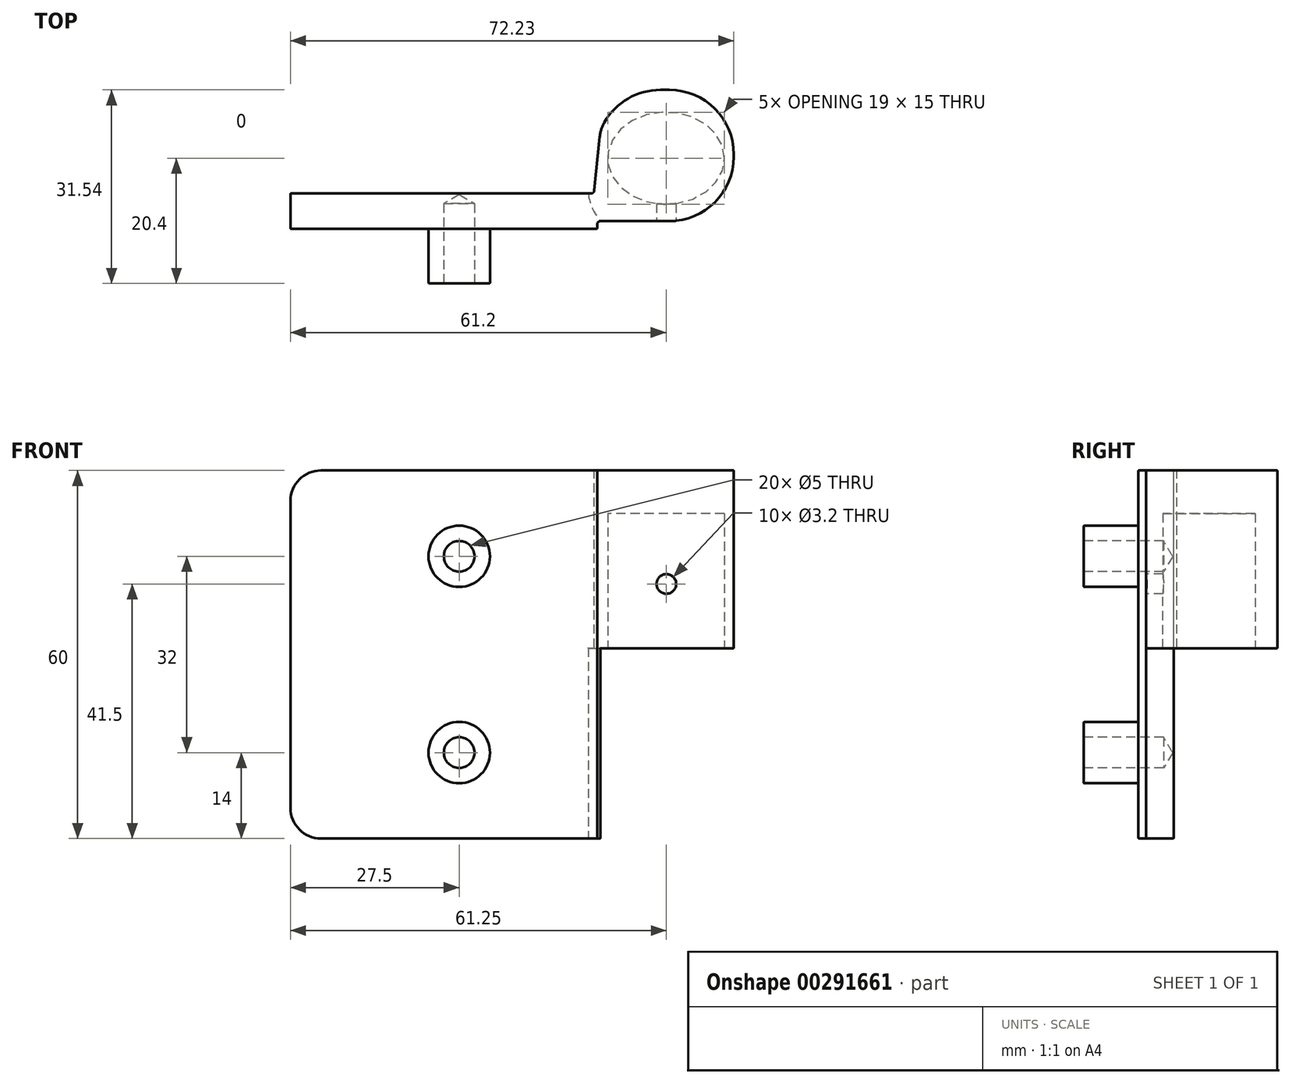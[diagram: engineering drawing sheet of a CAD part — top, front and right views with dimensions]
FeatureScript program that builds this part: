
annotation { "Feature Type Name" : "Feature", "Feature Type Description" : "" }
export const myFeature = defineFeature(function(context is Context, id is Id, definition is map)
    precondition{}
    {
        {
            var Q0;
            Q0=qCreatedBy(makeId("Front.planeOp"),FACE);
            var sketch = newSketch(context, id + "F0", { "sketchPlane" : qUnion([Q0])});
            skLineSegment(sketch, "E0", {"start": v(0, 0) * mm, "end": v(-48.5, 0) * mm});
            skLineSegment(sketch, "E1", {"start": v(-48.5, 0) * mm, "end": v(-48.5, -5.75) * mm});
            skLineSegment(sketch, "E2", {"start": v(-48.5, -5.75) * mm, "end": v(1.5, -5.75) * mm});
            skLineSegment(sketch, "E3", {"start": v(1.5, -5.75) * mm, "end": v(1.5, -5) * mm});
            skLineSegment(sketch, "E4", {"start": v(2, -4.5) * mm, "end": v(3.23, -4.5) * mm});
            skLineSegment(sketch, "E5", {"start": v(3.23, -4.5) * mm, "end": v(13.23, -4.5) * mm});
            skLineSegment(sketch, "E6", {"start": v(23.73, 6) * mm, "end": v(23.73, 6.4) * mm});
            skLineSegment(sketch, "E7", {"start": v(13.23, 16.9) * mm, "end": v(11.78, 16.9) * mm});
            skLineSegment(sketch, "E8", {"start": v(0.5, 0) * mm, "end": v(0, 0) * mm});
            skArc(sketch, "E9.filletArc", {"start": v(13.23, -4.5) * mm, "mid": v(20.66, -1.43) * mm, "end": v(23.73, 6) * mm});
            skArc(sketch, "E10.filletArc", {"start": v(23.73, 6.4) * mm, "mid": v(20.66, 13.82) * mm, "end": v(13.23, 16.9) * mm});
            skArc(sketch, "E11.filletArc", {"start": v(11.78, 16.9) * mm, "mid": v(6.5, 15.47) * mm, "end": v(2.65, 11.6) * mm});
            skArc(sketch, "E12.filletArc", {"start": v(0.5, 0) * mm, "mid": v(0.85, 0.15) * mm, "end": v(1, 0.5) * mm});
            skPoint(sketch, "E13.visualSharp", {"position": v(1.5, -4.5) * mm});
            skArc(sketch, "E13.filletArc", {"start": v(2, -4.5) * mm, "mid": v(1.65, -4.66) * mm, "end": v(1.5, -5) * mm});
            skLineSegment(sketch, "E14", {"start": v(1, 0.5) * mm, "end": v(1.9, 9.23) * mm});
            skPoint(sketch, "E15.visualSharp", {"position": v(2, 10.22) * mm});
            skArc(sketch, "E15.filletArc", {"start": v(2.65, 11.6) * mm, "mid": v(2.15, 10.45) * mm, "end": v(1.9, 9.23) * mm});
            skSolve(sketch);
        }
        {
            var Q0;
            Q0=makeQuery(id+"F0.imprint","IMPRINT",FACE,{"disambiguationData":[TD([[makeQuery(id+"F0.imprint","IMPRINT",EDGE,{"derivedFrom":sQuery(id+"F0.wireOp",EDGE,"E0")}),1.0]])]});
            extrude(context, id + "F1", {"entities" : qUnion([Q0]), "depth" : 60 * mm});
        }
        {
            var Q0;
            Q0=makeQuery(id+"F1.opExtrude","CAP_EDGE",EDGE,{"disambiguationData":[OSD([sQuery(id+"F0.wireOp",EDGE,"E1")])],"isStart":false});
            var Q1;
            Q1=makeQuery(id+"F1.opExtrude","CAP_EDGE",EDGE,{"disambiguationData":[OSD([sQuery(id+"F0.wireOp",EDGE,"E1")])],"isStart":true});
            fillet(context, id + "F2", {"entities" : qUnion([Q0, Q1]), "radius" : 5 * mm, "tangentPropagation" : true, "allowEdgeOverflow" : false});
        }
        {
            var Q0;
            Q0=makeQuery(id+"F1.opExtrude","SWEPT_FACE",FACE,{"disambiguationData":[OSD([sQuery(id+"F0.wireOp",EDGE,"E4"),sQuery(id+"F0.wireOp",EDGE,"E5")])]});
            var sketch = newSketch(context, id + "F3", { "sketchPlane" : qUnion([Q0])});
            skLineSegment(sketch, "E16.bottom", {"start": v(2, 60) * mm, "end": v(31.94, 60) * mm});
            skLineSegment(sketch, "E16.top", {"start": v(2, 29) * mm, "end": v(31.94, 29) * mm});
            skLineSegment(sketch, "E16.left", {"start": v(2, 60) * mm, "end": v(2, 29) * mm});
            skLineSegment(sketch, "E16.right", {"start": v(31.94, 60) * mm, "end": v(31.94, 29) * mm});
            skSolve(sketch);
        }
        {
            var Q0;
            Q0=qSketchRegion(id+"F3",true);
            extrude(context, id + "F4", {"entities" : qUnion([Q0]), "operationType" : NewBodyOperationType.REMOVE, "endBound" : BoundingType.THROUGH_ALL, "oppositeDirection" : true, "depth" : 25 * mm});
        }
        {
            var Q0;
            Q0=makeQuery(id+"F1.opExtrude","CAP_FACE",FACE,{"disambiguationData":[OSD([sQuery(id+"F0.wireOp",EDGE,"E0"),sQuery(id+"F0.wireOp",EDGE,"E1"),sQuery(id+"F0.wireOp",EDGE,"E2"),sQuery(id+"F0.wireOp",EDGE,"E3"),sQuery(id+"F0.wireOp",EDGE,"E4"),sQuery(id+"F0.wireOp",EDGE,"E5"),sQuery(id+"F0.wireOp",EDGE,"E6"),sQuery(id+"F0.wireOp",EDGE,"E7"),sQuery(id+"F0.wireOp",EDGE,"GG9Xp7Lx-0V8L-KjhP-dehT-RjXL1Wiv3JEy"),sQuery(id+"F0.wireOp",EDGE,"E8"),sQuery(id+"F0.wireOp",EDGE,"E9.filletArc"),sQuery(id+"F0.wireOp",EDGE,"E10.filletArc"),sQuery(id+"F0.wireOp",EDGE,"E11.filletArc"),sQuery(id+"F0.wireOp",EDGE,"E12.filletArc"),sQuery(id+"F0.wireOp",EDGE,"E13.filletArc")])],"isStart":false});
            var sketch = newSketch(context, id + "F5", { "sketchPlane" : qUnion([Q0])});
            skArc(sketch, "E17", {"start": v(0, 0) * mm, "mid": v(0.68, -2.4) * mm, "end": v(2, -4.5) * mm});
            skLineSegment(sketch, "E18", {"start": v(2, -4.5) * mm, "end": v(4.6, -0.03) * mm});
            skLineSegment(sketch, "E19", {"start": v(4.6, -0.03) * mm, "end": v(2.71, 13.2) * mm});
            skLineSegment(sketch, "E20", {"start": v(2.71, 13.2) * mm, "end": v(-1.4, 7.63) * mm});
            skLineSegment(sketch, "E21", {"start": v(0, 0) * mm, "end": v(-1.4, 7.63) * mm});
            skSolve(sketch);
        }
        {
            var Q0;
            Q0=qSketchRegion(id+"F5",true);
            extrude(context, id + "F6", {"entities" : qUnion([Q0]), "operationType" : NewBodyOperationType.REMOVE, "oppositeDirection" : true, "depth" : 31 * mm});
        }
        {
            var Q0;
            Q0=makeQuery(id+"F1.opExtrude","SWEPT_BODY",BODY,{"disambiguationData":[OSD([sQuery(id+"F0.wireOp",EDGE,"E0"),sQuery(id+"F0.wireOp",EDGE,"E1"),sQuery(id+"F0.wireOp",EDGE,"E2"),sQuery(id+"F0.wireOp",EDGE,"E3"),sQuery(id+"F0.wireOp",EDGE,"E4"),sQuery(id+"F0.wireOp",EDGE,"E5"),sQuery(id+"F0.wireOp",EDGE,"E6"),sQuery(id+"F0.wireOp",EDGE,"E7"),sQuery(id+"F0.wireOp",EDGE,"GG9Xp7Lx-0V8L-KjhP-dehT-RjXL1Wiv3JEy"),sQuery(id+"F0.wireOp",EDGE,"E8"),sQuery(id+"F0.wireOp",EDGE,"E9.filletArc"),sQuery(id+"F0.wireOp",EDGE,"E10.filletArc"),sQuery(id+"F0.wireOp",EDGE,"E11.filletArc"),sQuery(id+"F0.wireOp",EDGE,"E12.filletArc"),sQuery(id+"F0.wireOp",EDGE,"E13.filletArc")])]});
            var Q1;
            Q1=makeQuery(id+"F1.opExtrude","CAP_EDGE",EDGE,{"disambiguationData":[OSD([sQuery(id+"F0.wireOp",EDGE,"E0"),sQuery(id+"F0.wireOp",EDGE,"E8")])],"isStart":true});
            transform(context, id + "F7", {"entities" : qUnion([Q0]), "transformType" : TransformType.ROTATION, "transformAxis" : qUnion([Q1]), "angle" : 90 * degree, "makeCopy" : false});
        }
        {
            var Q0;
            Q0=makeQuery(id+"F1.opExtrude","SWEPT_FACE",FACE,{"disambiguationData":[OSD([sQuery(id+"F0.wireOp",EDGE,"E2")])]});
            var sketch = newSketch(context, id + "F8", { "sketchPlane" : qUnion([Q0])});
            skCircle(sketch, "E22", {"center": v(-21, 46) * mm, "radius": 5 * mm});
            skCircle(sketch, "E23", {"center": v(-21, 14) * mm, "radius": 5 * mm});
            skSolve(sketch);
        }
        {
            var Q0;
            Q0=qSketchRegion(id+"F8",true);
            extrude(context, id + "F9", {"entities" : qUnion([Q0]), "operationType" : NewBodyOperationType.ADD, "depth" : 8.9 * mm});
        }
        {
            var Q0;
            Q0=makeQuery(id+"F9.opExtrude","CAP_FACE",FACE,{"disambiguationData":[OSD([sQuery(id+"F8.wireOp",EDGE,"E22")])],"isStart":false});
            var sketch = newSketch(context, id + "F10", { "sketchPlane" : qUnion([Q0])});
            skCircle(sketch, "E24", {"center": v(-21, 46) * mm, "radius": 2.5 * mm});
            skSolve(sketch);
        }
        {
            var Q0;
            Q0=makeQuery(id+"F9.opExtrude","CAP_FACE",FACE,{"disambiguationData":[OSD([sQuery(id+"F8.wireOp",EDGE,"E23")])],"isStart":false});
            var sketch = newSketch(context, id + "F11", { "sketchPlane" : qUnion([Q0])});
            skCircle(sketch, "E25", {"center": v(-21, 14) * mm, "radius": 2.5 * mm});
            skSolve(sketch);
        }
        {
            var Q0;
            Q0=sQuery(id+"F10.wireOp",VERTEX,"E24.center");
            var Q1;
            Q1=makeQuery(id+"F1.opExtrude","SWEPT_BODY",BODY,{"disambiguationData":[OSD([sQuery(id+"F0.wireOp",EDGE,"E0"),sQuery(id+"F0.wireOp",EDGE,"E1"),sQuery(id+"F0.wireOp",EDGE,"E2"),sQuery(id+"F0.wireOp",EDGE,"E3"),sQuery(id+"F0.wireOp",EDGE,"E4"),sQuery(id+"F0.wireOp",EDGE,"E5"),sQuery(id+"F0.wireOp",EDGE,"E6"),sQuery(id+"F0.wireOp",EDGE,"E7"),sQuery(id+"F0.wireOp",EDGE,"GG9Xp7Lx-0V8L-KjhP-dehT-RjXL1Wiv3JEy"),sQuery(id+"F0.wireOp",EDGE,"E8"),sQuery(id+"F0.wireOp",EDGE,"E9.filletArc"),sQuery(id+"F0.wireOp",EDGE,"E10.filletArc"),sQuery(id+"F0.wireOp",EDGE,"E11.filletArc"),sQuery(id+"F0.wireOp",EDGE,"E12.filletArc"),sQuery(id+"F0.wireOp",EDGE,"E13.filletArc")])]});
            hole(context, id + "F12", {"style" : HoleStyle.SIMPLE, "endStyle" : HoleEndStyle.BLIND, "standardTappedOrClearance" : lookupTablePath({ "standard" : "ISO", "engagement" : "75%", "pitch" : "1 mm", "size" : "M6", "type" : "Tapped" }), "standardBlindInLast" : lookupTablePath({ "standard" : "ISO", "engagement" : "75%", "pitch" : "1 mm", "size" : "M6", "type" : "Tapped" }), "holeDiameter" : 5 * mm, "showTappedDepth" : true, "holeDepth" : 13 * mm, "tappedDepth" : 10 * mm, "tapClearance" : 3, "locations" : qUnion([Q0]), "scope" : qUnion([Q1]), "majorDiameter" : 6 * mm});
        }
        {
            var Q0;
            Q0=sQuery(id+"F11.wireOp",VERTEX,"E25.center");
            var Q1;
            Q1=makeQuery(id+"F1.opExtrude","SWEPT_BODY",BODY,{"disambiguationData":[OSD([sQuery(id+"F0.wireOp",EDGE,"E0"),sQuery(id+"F0.wireOp",EDGE,"E1"),sQuery(id+"F0.wireOp",EDGE,"E2"),sQuery(id+"F0.wireOp",EDGE,"E3"),sQuery(id+"F0.wireOp",EDGE,"E4"),sQuery(id+"F0.wireOp",EDGE,"E5"),sQuery(id+"F0.wireOp",EDGE,"E6"),sQuery(id+"F0.wireOp",EDGE,"E7"),sQuery(id+"F0.wireOp",EDGE,"GG9Xp7Lx-0V8L-KjhP-dehT-RjXL1Wiv3JEy"),sQuery(id+"F0.wireOp",EDGE,"E8"),sQuery(id+"F0.wireOp",EDGE,"E9.filletArc"),sQuery(id+"F0.wireOp",EDGE,"E10.filletArc"),sQuery(id+"F0.wireOp",EDGE,"E11.filletArc"),sQuery(id+"F0.wireOp",EDGE,"E12.filletArc"),sQuery(id+"F0.wireOp",EDGE,"E13.filletArc")])]});
            hole(context, id + "F13", {"style" : HoleStyle.SIMPLE, "endStyle" : HoleEndStyle.BLIND, "standardTappedOrClearance" : lookupTablePath({ "standard" : "ISO", "engagement" : "75%", "pitch" : "1 mm", "size" : "M6", "type" : "Tapped" }), "standardBlindInLast" : lookupTablePath({ "standard" : "ISO", "engagement" : "75%", "pitch" : "1 mm", "size" : "M6", "type" : "Tapped" }), "holeDiameter" : 5 * mm, "showTappedDepth" : true, "holeDepth" : 13 * mm, "tappedDepth" : 10 * mm, "tapClearance" : 3, "locations" : qUnion([Q0]), "scope" : qUnion([Q1]), "majorDiameter" : 6 * mm});
        }
        {
            var Q0;
            Q0=makeQuery(id+"F6.boolean.opBoolean","MERGE",FACE,{"derivedFrom":[makeQuery(id+"F4.boolean.opBoolean","COPY",FACE,{"derivedFrom":makeQuery(id+"F4.opExtrude","SWEPT_FACE",FACE,{"disambiguationData":[OSD([sQuery(id+"F3.wireOp",EDGE,"E16.top")])]})}),makeQuery(id+"F6.opExtrude","CAP_FACE",FACE,{"disambiguationData":[OSD([sQuery(id+"F5.wireOp",EDGE,"E17"),sQuery(id+"F5.wireOp",EDGE,"E18"),sQuery(id+"F5.wireOp",EDGE,"E19"),sQuery(id+"F5.wireOp",EDGE,"E20"),sQuery(id+"F5.wireOp",EDGE,"E21")])],"isStart":false})]});
            var sketch = newSketch(context, id + "F14", { "sketchPlane" : qUnion([Q0])});
            skEllipse(sketch, "E26", {"center": v(12.7, 5.75) * mm, "majorRadius": 9.5 * mm, "minorRadius": 7.5 * mm, "majorAxis": v(1, 0)});
            skSolve(sketch);
        }
        {
            var Q0;
            Q0=qSketchRegion(id+"F14",true);
            extrude(context, id + "F15", {"entities" : qUnion([Q0]), "operationType" : NewBodyOperationType.REMOVE, "oppositeDirection" : true, "depth" : 22 * mm});
        }
        {
            var Q0;
            Q0=makeQuery(id+"F1.opExtrude","SWEPT_FACE",FACE,{"disambiguationData":[OSD([sQuery(id+"F0.wireOp",EDGE,"E4"),sQuery(id+"F0.wireOp",EDGE,"E5")])]});
            var sketch = newSketch(context, id + "F16", { "sketchPlane" : qUnion([Q0])});
            skCircle(sketch, "E27", {"center": v(12.75, 18.5) * mm, "radius": 1.5 * mm});
            skSolve(sketch);
        }
        {
            var Q0;
            Q0=sQuery(id+"F16.wireOp",VERTEX,"E27.center");
            var Q1;
            Q1=makeQuery(id+"F1.opExtrude","SWEPT_BODY",BODY,{"disambiguationData":[OSD([sQuery(id+"F0.wireOp",EDGE,"E0"),sQuery(id+"F0.wireOp",EDGE,"E1"),sQuery(id+"F0.wireOp",EDGE,"E2"),sQuery(id+"F0.wireOp",EDGE,"E3"),sQuery(id+"F0.wireOp",EDGE,"E4"),sQuery(id+"F0.wireOp",EDGE,"E5"),sQuery(id+"F0.wireOp",EDGE,"E6"),sQuery(id+"F0.wireOp",EDGE,"E7"),sQuery(id+"F0.wireOp",EDGE,"E8"),sQuery(id+"F0.wireOp",EDGE,"E9.filletArc"),sQuery(id+"F0.wireOp",EDGE,"E10.filletArc"),sQuery(id+"F0.wireOp",EDGE,"E11.filletArc"),sQuery(id+"F0.wireOp",EDGE,"E12.filletArc"),sQuery(id+"F0.wireOp",EDGE,"E13.filletArc"),sQuery(id+"F0.wireOp",EDGE,"E14"),sQuery(id+"F0.wireOp",EDGE,"E15.filletArc")])]});
            hole(context, id + "F17", {"style" : HoleStyle.SIMPLE, "endStyle" : HoleEndStyle.BLIND, "standardTappedOrClearance" : lookupTablePath({ "standard" : "ISO", "engagement" : "75%", "pitch" : "0.75 mm", "size" : "M4", "type" : "Tapped" }), "standardBlindInLast" : lookupTablePath({ "standard" : "ISO", "engagement" : "75%", "pitch" : "0.75 mm", "size" : "M4", "type" : "Tapped" }), "holeDiameter" : 3.2 * mm, "showTappedDepth" : true, "holeDepth" : 12.25 * mm, "tappedDepth" : 10 * mm, "tapClearance" : 3, "locations" : qUnion([Q0]), "scope" : qUnion([Q1])});
        }
        {
            var Q0;
            Q0=makeQuery(id+"F15.boolean.opBoolean","COPY",EDGE,{"derivedFrom":makeQuery(id+"F15.opExtrude","CAP_EDGE",EDGE,{"disambiguationData":[OSD([sQuery(id+"F14.wireOp",EDGE,"E26")])],"isStart":true})});
            var Q1;
            Q1=makeQuery(id+"F6.boolean.opBoolean","INTERSECT",EDGE,{"derivedFrom":[makeQuery(id+"F1.opExtrude","SWEPT_FACE",FACE,{"disambiguationData":[OSD([sQuery(id+"F0.wireOp",EDGE,"E12.filletArc")])]}),makeQuery(id+"F6.opExtrude","CAP_FACE",FACE,{"disambiguationData":[OSD([sQuery(id+"F5.wireOp",EDGE,"E17"),sQuery(id+"F5.wireOp",EDGE,"E18"),sQuery(id+"F5.wireOp",EDGE,"E19"),sQuery(id+"F5.wireOp",EDGE,"E20"),sQuery(id+"F5.wireOp",EDGE,"E21")])],"isStart":false})]});
            var Q2;
            Q2=makeQuery(id+"F6.boolean.opBoolean","INTERSECT",EDGE,{"derivedFrom":[makeQuery(id+"F1.opExtrude","SWEPT_FACE",FACE,{"disambiguationData":[OSD([sQuery(id+"F0.wireOp",EDGE,"E14")])]}),makeQuery(id+"F6.opExtrude","CAP_FACE",FACE,{"disambiguationData":[OSD([sQuery(id+"F5.wireOp",EDGE,"E17"),sQuery(id+"F5.wireOp",EDGE,"E18"),sQuery(id+"F5.wireOp",EDGE,"E19"),sQuery(id+"F5.wireOp",EDGE,"E20"),sQuery(id+"F5.wireOp",EDGE,"E21")])],"isStart":false})]});
            var Q3;
            Q3=makeQuery(id+"F1.opExtrude","CAP_EDGE",EDGE,{"disambiguationData":[OSD([sQuery(id+"F0.wireOp",EDGE,"E0"),sQuery(id+"F0.wireOp",EDGE,"E8")])],"isStart":false});
            var Q4;
            Q4=makeQuery(id+"F1.opExtrude","CAP_EDGE",EDGE,{"disambiguationData":[OSD([sQuery(id+"F0.wireOp",EDGE,"E2")])],"isStart":false});
            var Q5;
            Q5=makeQuery(id+"F1.opExtrude","CAP_EDGE",EDGE,{"disambiguationData":[OSD([sQuery(id+"F0.wireOp",EDGE,"E14")])],"isStart":true});
            var Q6;
            Q6=makeQuery(id+"F1.opExtrude","SWEPT_EDGE",EDGE,{"disambiguationData":[OSD([sQuery(id+"F0.wireOp",EDGE,"E2"),sQuery(id+"F0.wireOp",EDGE,"E3")])]});
            var Q7;
            Q7=makeQuery(id+"F6.boolean.opBoolean","COPY",EDGE,{"derivedFrom":makeQuery(id+"F6.opExtrude","SWEPT_EDGE",EDGE,{"disambiguationData":[OSD([sQuery(id+"F0.wireOp",EDGE,"E0"),sQuery(id+"F0.wireOp",EDGE,"E8"),sQuery(id+"F5.wireOp",EDGE,"E17"),sQuery(id+"F5.wireOp",EDGE,"E21")])]})});
            var Q8;
            Q8=makeQuery(id+"F6.boolean.opBoolean","COPY",EDGE,{"derivedFrom":makeQuery(id+"F6.opExtrude","CAP_EDGE",EDGE,{"disambiguationData":[OSD([sQuery(id+"F5.wireOp",EDGE,"E17")])],"isStart":true})});
            var Q9;
            Q9=makeQuery(id+"F1.opExtrude","CAP_EDGE",EDGE,{"disambiguationData":[OSD([sQuery(id+"F0.wireOp",EDGE,"E13.filletArc")])],"isStart":false});
            var Q10;
            Q10=makeQuery(id+"F9.opExtrude","CAP_EDGE",EDGE,{"disambiguationData":[OSD([sQuery(id+"F8.wireOp",EDGE,"E22")])],"isStart":false});
            var Q11;
            Q11=makeQuery(id+"F9.opExtrude","CAP_EDGE",EDGE,{"disambiguationData":[OSD([sQuery(id+"F8.wireOp",EDGE,"E23")])],"isStart":false});
            var Q12;
            Q12=makeQuery(id+"F9.opExtrude","CAP_EDGE",EDGE,{"disambiguationData":[OSD([sQuery(id+"F8.wireOp",EDGE,"E22")])],"isStart":true});
            var Q13;
            Q13=makeQuery(id+"F9.opExtrude","CAP_EDGE",EDGE,{"disambiguationData":[OSD([sQuery(id+"F8.wireOp",EDGE,"E23")])],"isStart":true});
            fillet(context, id + "F18", {"entities" : qUnion([Q0, Q1, Q2, Q3, Q4, Q5, Q6, Q7, Q8, Q9, Q10, Q11, Q12, Q13]), "radius" : 0.1 * mm, "tangentPropagation" : true, "allowEdgeOverflow" : false});
        }
        {
            var Q0;
            Q0=makeQuery(id+"F1.opExtrude","SWEPT_BODY",BODY,{"disambiguationData":[OSD([sQuery(id+"F0.wireOp",EDGE,"E0"),sQuery(id+"F0.wireOp",EDGE,"E1"),sQuery(id+"F0.wireOp",EDGE,"E2"),sQuery(id+"F0.wireOp",EDGE,"E3"),sQuery(id+"F0.wireOp",EDGE,"E4"),sQuery(id+"F0.wireOp",EDGE,"E5"),sQuery(id+"F0.wireOp",EDGE,"E6"),sQuery(id+"F0.wireOp",EDGE,"E7"),sQuery(id+"F0.wireOp",EDGE,"E8"),sQuery(id+"F0.wireOp",EDGE,"E9.filletArc"),sQuery(id+"F0.wireOp",EDGE,"E10.filletArc"),sQuery(id+"F0.wireOp",EDGE,"E11.filletArc"),sQuery(id+"F0.wireOp",EDGE,"E12.filletArc"),sQuery(id+"F0.wireOp",EDGE,"E13.filletArc"),sQuery(id+"F0.wireOp",EDGE,"E14"),sQuery(id+"F0.wireOp",EDGE,"E15.filletArc")])]});
            var Q1;
            {var subQ0=sQuery(id+"F0.wireOp",EDGE,"E2");Q1=makeQuery(id+"F18.opFillet","BLEND_EDGE",EDGE,{"blendedFrom":[makeQuery(id+"F1.opExtrude","CAP_EDGE",EDGE,{"disambiguationData":[OSD([subQ0])],"isStart":true}),makeQuery(id+"F1.opExtrude","CAP_FACE",FACE,{"disambiguationData":[OSD([sQuery(id+"F0.wireOp",EDGE,"E0"),sQuery(id+"F0.wireOp",EDGE,"E1"),subQ0,sQuery(id+"F0.wireOp",EDGE,"E3"),sQuery(id+"F0.wireOp",EDGE,"E4"),sQuery(id+"F0.wireOp",EDGE,"E5"),sQuery(id+"F0.wireOp",EDGE,"E6"),sQuery(id+"F0.wireOp",EDGE,"E7"),sQuery(id+"F0.wireOp",EDGE,"E8"),sQuery(id+"F0.wireOp",EDGE,"E9.filletArc"),sQuery(id+"F0.wireOp",EDGE,"E10.filletArc"),sQuery(id+"F0.wireOp",EDGE,"E11.filletArc"),sQuery(id+"F0.wireOp",EDGE,"E12.filletArc"),sQuery(id+"F0.wireOp",EDGE,"E13.filletArc"),sQuery(id+"F0.wireOp",EDGE,"E14"),sQuery(id+"F0.wireOp",EDGE,"E15.filletArc")])],"isStart":true})],"blendedInto":[makeQuery(id+"F1.opExtrude","CAP_FACE",FACE,{"disambiguationData":[OSD([sQuery(id+"F0.wireOp",EDGE,"E0"),sQuery(id+"F0.wireOp",EDGE,"E1"),subQ0,sQuery(id+"F0.wireOp",EDGE,"E3"),sQuery(id+"F0.wireOp",EDGE,"E4"),sQuery(id+"F0.wireOp",EDGE,"E5"),sQuery(id+"F0.wireOp",EDGE,"E6"),sQuery(id+"F0.wireOp",EDGE,"E7"),sQuery(id+"F0.wireOp",EDGE,"E8"),sQuery(id+"F0.wireOp",EDGE,"E9.filletArc"),sQuery(id+"F0.wireOp",EDGE,"E10.filletArc"),sQuery(id+"F0.wireOp",EDGE,"E11.filletArc"),sQuery(id+"F0.wireOp",EDGE,"E12.filletArc"),sQuery(id+"F0.wireOp",EDGE,"E13.filletArc"),sQuery(id+"F0.wireOp",EDGE,"E14"),sQuery(id+"F0.wireOp",EDGE,"E15.filletArc")])],"isStart":true})]});}
            var Q2;
            {var subQ0=sQuery(id+"F0.wireOp",EDGE,"E2");Q2=makeQuery(id+"F18.opFillet","BLEND_EDGE",EDGE,{"blendedFrom":[makeQuery(id+"F1.opExtrude","CAP_EDGE",EDGE,{"disambiguationData":[OSD([subQ0])],"isStart":true}),makeQuery(id+"F1.opExtrude","SWEPT_FACE",FACE,{"disambiguationData":[OSD([subQ0])]})],"blendedInto":[makeQuery(id+"F1.opExtrude","SWEPT_FACE",FACE,{"disambiguationData":[OSD([subQ0])]})]});}
            transform(context, id + "F19", {"entities" : qUnion([Q0]), "transformType" : TransformType.TRANSLATION_DISTANCE, "transformDirection" : qUnion([Q2]), "distance" : 35 * mm, "oppositeDirection" : true, "makeCopy" : false});
        }
        {
            var Q0;
            Q0=makeQuery(id+"F1.opExtrude","SWEPT_BODY",BODY,{"disambiguationData":[OSD([sQuery(id+"F0.wireOp",EDGE,"E0"),sQuery(id+"F0.wireOp",EDGE,"E1"),sQuery(id+"F0.wireOp",EDGE,"E2"),sQuery(id+"F0.wireOp",EDGE,"E3"),sQuery(id+"F0.wireOp",EDGE,"E4"),sQuery(id+"F0.wireOp",EDGE,"E5"),sQuery(id+"F0.wireOp",EDGE,"E6"),sQuery(id+"F0.wireOp",EDGE,"E7"),sQuery(id+"F0.wireOp",EDGE,"E8"),sQuery(id+"F0.wireOp",EDGE,"E9.filletArc"),sQuery(id+"F0.wireOp",EDGE,"E10.filletArc"),sQuery(id+"F0.wireOp",EDGE,"E11.filletArc"),sQuery(id+"F0.wireOp",EDGE,"E12.filletArc"),sQuery(id+"F0.wireOp",EDGE,"E13.filletArc"),sQuery(id+"F0.wireOp",EDGE,"E14"),sQuery(id+"F0.wireOp",EDGE,"E15.filletArc")])]});
            var Q1;
            Q1=qCreatedBy(makeId("Right.planeOp"),FACE);
            mirror(context, id + "F20", {"entities" : qUnion([Q0]), "mirrorPlane" : qUnion([Q1])});
        }
        {
            var Q0;
            Q0=makeQuery(id+"F1.opExtrude","SWEPT_BODY",BODY,{"disambiguationData":[OSD([sQuery(id+"F0.wireOp",EDGE,"E0"),sQuery(id+"F0.wireOp",EDGE,"E1"),sQuery(id+"F0.wireOp",EDGE,"E2"),sQuery(id+"F0.wireOp",EDGE,"E3"),sQuery(id+"F0.wireOp",EDGE,"E4"),sQuery(id+"F0.wireOp",EDGE,"E5"),sQuery(id+"F0.wireOp",EDGE,"E6"),sQuery(id+"F0.wireOp",EDGE,"E7"),sQuery(id+"F0.wireOp",EDGE,"E8"),sQuery(id+"F0.wireOp",EDGE,"E9.filletArc"),sQuery(id+"F0.wireOp",EDGE,"E10.filletArc"),sQuery(id+"F0.wireOp",EDGE,"E11.filletArc"),sQuery(id+"F0.wireOp",EDGE,"E12.filletArc"),sQuery(id+"F0.wireOp",EDGE,"E13.filletArc"),sQuery(id+"F0.wireOp",EDGE,"E14"),sQuery(id+"F0.wireOp",EDGE,"E15.filletArc")])]});
            deleteBodies(context, id + "F21", {"entities" : qUnion([Q0])});
        }
        {
            var Q0;
            Q0=makeQuery(id+"F20.opPattern","COPY",BODY,{"derivedFrom":makeQuery(id+"F1.opExtrude","SWEPT_BODY",BODY,{"disambiguationData":[OSD([sQuery(id+"F0.wireOp",EDGE,"E0"),sQuery(id+"F0.wireOp",EDGE,"E1"),sQuery(id+"F0.wireOp",EDGE,"E2"),sQuery(id+"F0.wireOp",EDGE,"E3"),sQuery(id+"F0.wireOp",EDGE,"E4"),sQuery(id+"F0.wireOp",EDGE,"E5"),sQuery(id+"F0.wireOp",EDGE,"E6"),sQuery(id+"F0.wireOp",EDGE,"E7"),sQuery(id+"F0.wireOp",EDGE,"E8"),sQuery(id+"F0.wireOp",EDGE,"E9.filletArc"),sQuery(id+"F0.wireOp",EDGE,"E10.filletArc"),sQuery(id+"F0.wireOp",EDGE,"E11.filletArc"),sQuery(id+"F0.wireOp",EDGE,"E12.filletArc"),sQuery(id+"F0.wireOp",EDGE,"E13.filletArc"),sQuery(id+"F0.wireOp",EDGE,"E14"),sQuery(id+"F0.wireOp",EDGE,"E15.filletArc")])]}),"instanceName":"1"});
            var Q1;
            {var subQ0=sQuery(id+"F0.wireOp",EDGE,"E1");Q1=makeQuery(id+"F20.opPattern","COPY",EDGE,{"derivedFrom":makeQuery(id+"F2.opFillet","BLEND_EDGE",EDGE,{"blendedFrom":[makeQuery(id+"F1.opExtrude","CAP_EDGE",EDGE,{"disambiguationData":[OSD([subQ0])],"isStart":false}),makeQuery(id+"F1.opExtrude","CAP_FACE",FACE,{"disambiguationData":[OSD([sQuery(id+"F0.wireOp",EDGE,"E0"),subQ0,sQuery(id+"F0.wireOp",EDGE,"E2"),sQuery(id+"F0.wireOp",EDGE,"E3"),sQuery(id+"F0.wireOp",EDGE,"E4"),sQuery(id+"F0.wireOp",EDGE,"E5"),sQuery(id+"F0.wireOp",EDGE,"E6"),sQuery(id+"F0.wireOp",EDGE,"E7"),sQuery(id+"F0.wireOp",EDGE,"E8"),sQuery(id+"F0.wireOp",EDGE,"E9.filletArc"),sQuery(id+"F0.wireOp",EDGE,"E10.filletArc"),sQuery(id+"F0.wireOp",EDGE,"E11.filletArc"),sQuery(id+"F0.wireOp",EDGE,"E12.filletArc"),sQuery(id+"F0.wireOp",EDGE,"E13.filletArc"),sQuery(id+"F0.wireOp",EDGE,"E14"),sQuery(id+"F0.wireOp",EDGE,"E15.filletArc")])],"isStart":false})],"blendedInto":[makeQuery(id+"F1.opExtrude","CAP_FACE",FACE,{"disambiguationData":[OSD([sQuery(id+"F0.wireOp",EDGE,"E0"),subQ0,sQuery(id+"F0.wireOp",EDGE,"E2"),sQuery(id+"F0.wireOp",EDGE,"E3"),sQuery(id+"F0.wireOp",EDGE,"E4"),sQuery(id+"F0.wireOp",EDGE,"E5"),sQuery(id+"F0.wireOp",EDGE,"E6"),sQuery(id+"F0.wireOp",EDGE,"E7"),sQuery(id+"F0.wireOp",EDGE,"E8"),sQuery(id+"F0.wireOp",EDGE,"E9.filletArc"),sQuery(id+"F0.wireOp",EDGE,"E10.filletArc"),sQuery(id+"F0.wireOp",EDGE,"E11.filletArc"),sQuery(id+"F0.wireOp",EDGE,"E12.filletArc"),sQuery(id+"F0.wireOp",EDGE,"E13.filletArc"),sQuery(id+"F0.wireOp",EDGE,"E14"),sQuery(id+"F0.wireOp",EDGE,"E15.filletArc")])],"isStart":false})]}),"instanceName":"1"});}
            transform(context, id + "F22", {"entities" : qUnion([Q0]), "transformType" : TransformType.ROTATION, "transformAxis" : qUnion([Q1]), "angle" : 180 * degree, "makeCopy" : false});
        }
    });
